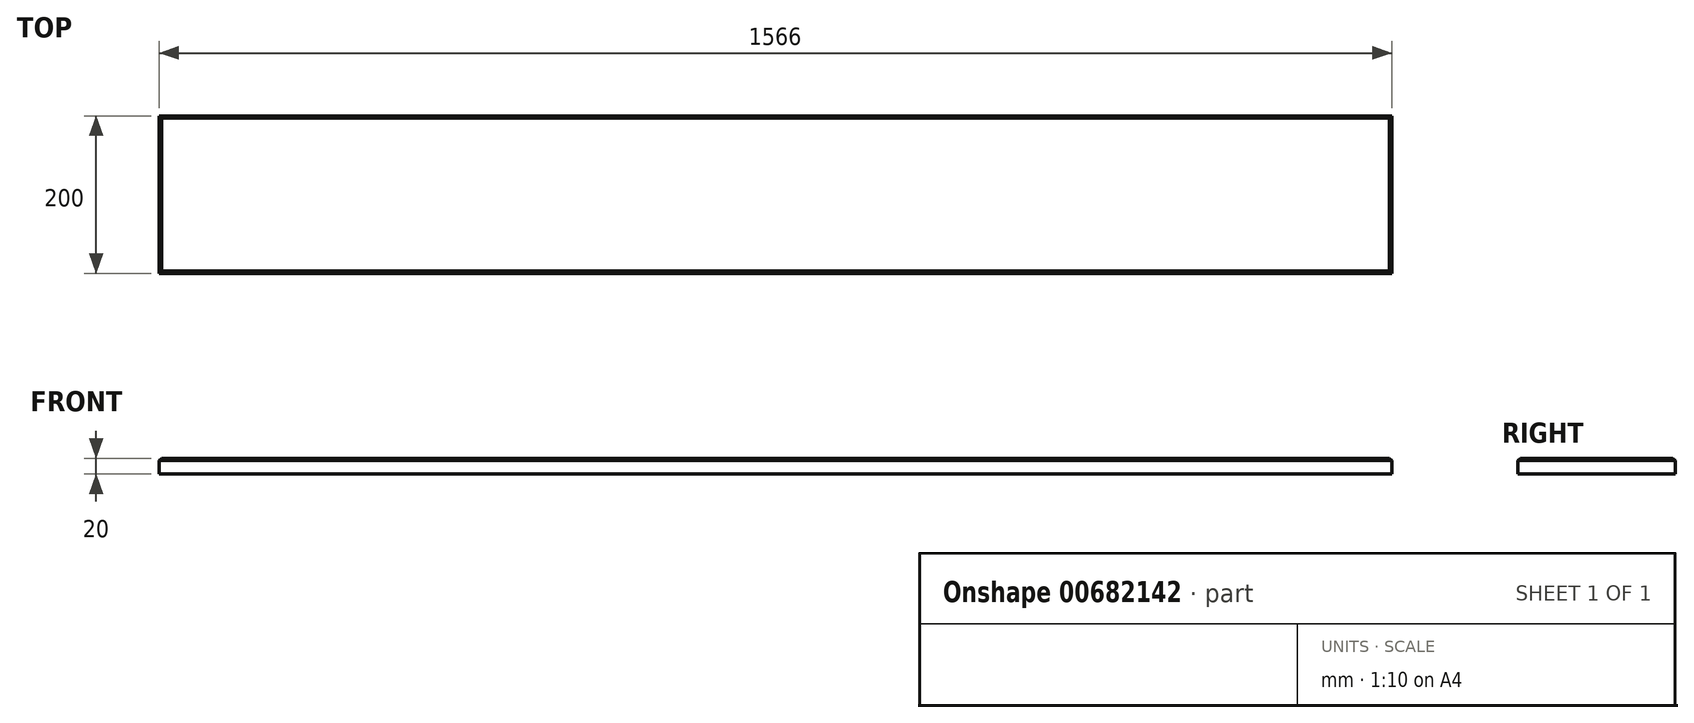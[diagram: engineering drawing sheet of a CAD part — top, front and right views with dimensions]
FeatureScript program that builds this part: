
annotation { "Feature Type Name" : "Feature", "Feature Type Description" : "" }
export const myFeature = defineFeature(function(context is Context, id is Id, definition is map)
    precondition{}
    {
        {
            var Q0;
            Q0=qCreatedBy(makeId("Top.planeOp"),FACE);
            var sketch = newSketch(context, id + "F0", { "sketchPlane" : qUnion([Q0])});
            skLineSegment(sketch, "E0.bottom", {"start": v(-783, 100) * mm, "end": v(783, 100) * mm});
            skLineSegment(sketch, "E0.top", {"start": v(-783, -100) * mm, "end": v(783, -100) * mm});
            skLineSegment(sketch, "E0.left", {"start": v(-783, 100) * mm, "end": v(-783, -100) * mm});
            skLineSegment(sketch, "E0.right", {"start": v(783, 100) * mm, "end": v(783, -100) * mm});
            skPoint(sketch, "E0.middle", {"position": v(0, 0) * mm});
            skSolve(sketch);
        }
        {
            var Q0;
            Q0=qSketchRegion(id+"F0",true);
            extrude(context, id + "F1", {"entities" : qUnion([Q0]), "depth" : 20 * mm, "offsetDistance" : 25 * mm});
        }
        {
            var Q0;
            Q0=makeQuery(id+"F1.opExtrude","CAP_FACE",FACE,{"disambiguationData":[OSD([sQuery(id+"F0.wireOp",EDGE,"E0.bottom"),sQuery(id+"F0.wireOp",EDGE,"E0.top"),sQuery(id+"F0.wireOp",EDGE,"E0.left"),sQuery(id+"F0.wireOp",EDGE,"E0.right")])],"isStart":false});
            chamfer(context, id + "F2", {"entities" : qUnion([Q0]), "width" : 3 * mm, "tangentPropagation" : true});
        }
    });
